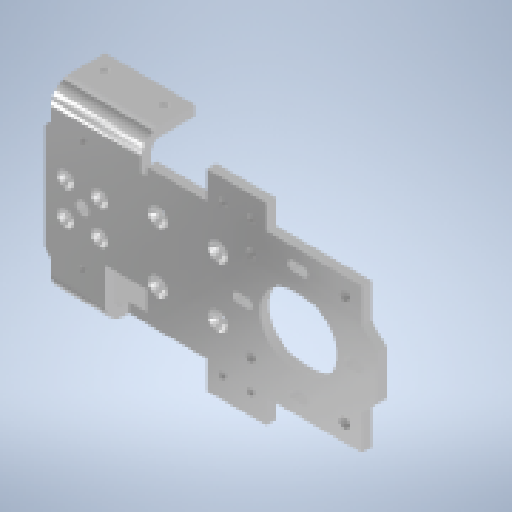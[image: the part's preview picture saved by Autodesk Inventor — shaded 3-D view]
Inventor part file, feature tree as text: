
AUTODESK INVENTOR PART (.ipt)
format: ipt  version: 2024 (Build 280153000, 153)  size: 621,056 bytes
history: native  units: mm
features: sheet_metal_op x17, hole x9, other x8, sketch x5, plane x5, fillet x4, mirror x3, extrude x3, projected_geometry x3
ambient origin geometry x8: Origin, YZ Plane, XZ Plane, XY Plane, X Axis, Y Axis, Z Axis, Center Point
bodies: Solid1 (feature_tree)
feature tree (57):
  sketch  "Sketch1"  dims[d0=27.0mm d1=45.4mm]
  sheet_metal_op  "Face1"
  hole  "Hole1"  [1 undecoded]
  hole  "Hole2"  [1 undecoded]
  hole  "Hole3"  [1 undecoded]
  hole  "Hole4"  [1 undecoded]
  sheet_metal_op  "Face3"
  hole  "Hole5"  [1 undecoded]
  sheet_metal_op  "Face4"
  hole  "Hole6"  [1 undecoded]
  mirror  "Mirror1"
  hole  "Hole7"  [1 undecoded]
  mirror  "Mirror2"
  sketch  "Sketch5"  dims[d2=37.0mm d3=19.5mm]
  sheet_metal_op  "Face5"
  extrude  "Extrusion1"  Depth=1.0mm
  plane  "Work Plane1"
  sheet_metal_op  "Flange1"
  plane  "Work Plane2"
  sheet_metal_op  "Face6"
  hole  "Hole8"  [1 undecoded]
  mirror  "Mirror4"
  sheet_metal_op  "Face7"
  sheet_metal_op  "Flange2"
  extrude  "Extrusion2"  Depth=1.0mm
  hole  "Hole9"  [1 undecoded]
  plane  "Work Plane3"
  plane  "Work Plane5"
  extrude  "Extrusion3"  Depth=22.25mm
  fillet  "Fillet1"  Radius=3.5mm
  fillet  "Fillet2"  Radius=22.0mm
  fillet  "Fillet3"  Radius=100.0mm
  fillet  "Fillet4"  Radius=30.0mm
  other  "Plate1"
  other  "Plate3"
  sheet_metal_op  "Bend2"
  other  "Plate4"
  sheet_metal_op  "Bend3"
  other  "Plate5"
  sheet_metal_op  "Bend4"
  sketch  "Sketch6"  dims[d4=16.0mm d5=35.0mm]
  other  "Plate6"
  sheet_metal_op  "Bend5"
  sheet_metal_op  "Corner1"
  projected_geometry  "Projected Loop1"
  other  "Plate7"
  sheet_metal_op  "Bend6"
  other  "Plate8"
  sheet_metal_op  "Bend7"
  sketch  "Sketch9"  dims[d6=12.75mm d7=3.175mm]
  other  "Plate9"
  sheet_metal_op  "Bend8"
  sheet_metal_op  "Corner2"
  projected_geometry  "Projected Loop2"
  plane  "Work Plane4"
  sketch  "Sketch12"  dims[d8=20.0mm d9=20.0mm d10=3.4mm d11=8.0mm d12=6.3mm d13=2.0mm d14=90.0deg d15=3.175mm d16=20.594885mm d17=2.9mm d18=8.0mm d19=5.5mm d20=2.0mm d21=90.0deg d22=3.175mm d23=20.594885mm d24=2.459mm d25=6.0mm d26=5.5mm d27=2.0mm d28=90.0deg d29=3.175mm d30=20.594885mm d31=4.5mm d32=6.0mm d33=5.5mm d34=2.0mm d35=90.0deg d36=3.175mm d37=20.594885mm d50=26.0mm d51=1.6mm d52=22.25mm d53=3.5mm d55=22.0mm d56=100.0mm d57=30.0mm d58=10.0mm d59=13.0mm d60=13.0mm d61=4.0mm d62=4.0mm d63=35.2mm d64=14.0mm d65=12.22mm d66=0.63mm d67=37.0mm d68=15.0mm d69=135.0deg d70=8.5mm d76=5.0mm d78=3.175mm d79=3.175mm d80=1.5875mm d81=6.35mm d82=3.175mm d83=3.242mm d84=8.0mm d85=5.5mm d86=2.0mm d87=90.0deg d88=11.8mm d89=20.594885mm d92=19.8mm d93=10.0mm d94=9.5mm d95=3.4mm d96=7.0mm d97=32.0mm d98=3.175mm d99=3.175mm d100=1.5875mm d101=6.35mm d102=3.175mm d103=2.459mm d104=6.0mm d105=5.5mm d106=2.0mm d107=90.0deg d108=8.8mm d109=20.594885mm d110=5.615224mm d111=5.615224mm d112=3.242mm d113=8.0mm d114=5.5mm d115=2.0mm d116=90.0deg d117=11.8mm d118=20.594885mm d119=23.0mm d120=48.0mm d121=7.0mm d122=35.0mm d124=7.0mm d125=4.5mm d126=3.175mm d127=3.175mm d128=1.5875mm d129=6.35mm d130=3.175mm d131=27.0mm d132=3.175mm d133=1.5875mm d134=6.35mm d135=3.175mm d136=10.0mm d137=90.0deg d138=3.175mm d139=12.7mm d140=3.175mm d141=3.175mm d142=2.25mm d143=30.0mm d144=2.0mm d147=45.0deg d148=3.0mm d149=0.0mm d150=0.0mm d151=1.0mm d152=-18.0mm d154=5.0mm d155=3.175mm d156=3.175mm d157=1.5875mm d158=6.35mm d159=3.175mm d160=2.459mm d161=6.0mm d162=5.5mm d163=2.0mm d164=90.0deg d165=8.8mm d166=20.594885mm d167=5.0mm d168=8.5mm d169=30.0deg d170=3.175mm d171=3.175mm d172=1.5875mm d173=6.35mm d174=3.175mm d175=3.175mm d176=1.5875mm d177=6.35mm d178=3.175mm d179=25.0mm d180=90.0deg d181=3.175mm d182=12.7mm d183=3.175mm d184=3.175mm d185=15.0mm d186=120.0deg d187=10.0mm d188=0.0mm d189=8.2mm d190=6.0mm d191=5.5mm d192=2.0mm d193=90.0deg d194=8.8mm d195=20.594885mm d196=13.0mm d197=6.35mm d198=10.0mm d199=14.0mm d200=8.0mm d201=0.0mm d202=1.0mm d203=1.0mm d204=1.0mm d205=1.0mm]
  projected_geometry  "Projected Loop3"
note: 9 required parameter values undecoded (feature->parameter linkage not recoverable at this tier; creation-order binding heuristic only, values carry confidence <= 0.55)
